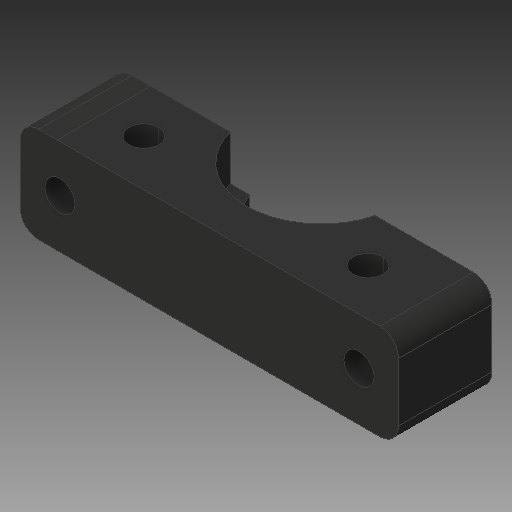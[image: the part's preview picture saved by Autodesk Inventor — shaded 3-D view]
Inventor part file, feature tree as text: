
AUTODESK INVENTOR PART (.ipt)
format: ipt  version: 2018 (Build 220112000, 112)  size: 193,024 bytes
history: native  units: mm
features: sketch x9, other x3
ambient origin geometry x8: Origin, YZ Plane, XZ Plane, XY Plane, X Axis, Y Axis, Z Axis, Center Point
bodies: Solid1 (feature_tree)
feature tree (12):
  other  "Hotend Clamp P2.ipt"
  other  "Solid1::Hotend Clamp P2.ipt"
  other  "TaggingFeature1"
  sketch  "Sketch1"  dims[d0=10.0mm]
  sketch  "Sketch2"
  sketch  "Sketch3"
  sketch  "Sketch4"
  sketch  "Sketch5"
  sketch  "Sketch6"
  sketch  "Sketch7"
  sketch  "Sketch8"
  sketch  "Sketch9"
